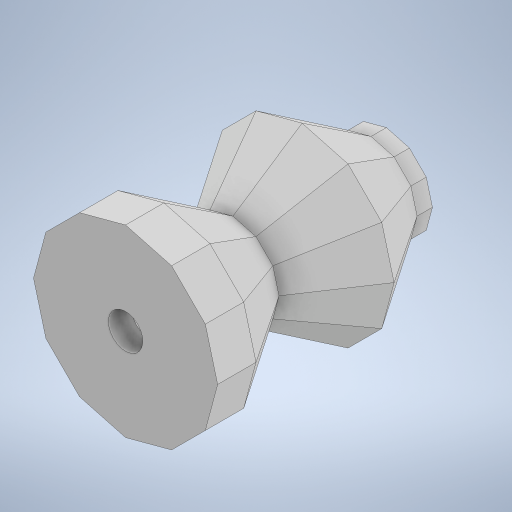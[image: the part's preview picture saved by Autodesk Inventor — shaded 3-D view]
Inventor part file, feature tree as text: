
AUTODESK INVENTOR PART (.ipt)
format: ipt  version: 2023 (Build 270158000, 158)  size: 354,304 bytes
history: native  units: in
note: dims shown in document units (in); Inventor stores cm internally (conversion verified against a paired STEP export)
features: sketch x6, extrude x4, projected_geometry x3, other x2, mirror x2, loft x1, shell x1
ambient origin geometry x8: Origin, YZ Plane, XZ Plane, XY Plane, X Axis, Y Axis, Z Axis, Center Point
bodies: Body1 (feature_tree)
feature tree (19):
  other  "솔리드1"
  sketch  "스케치1"
  other  "작업 평면1"
  loft  "로프트1"
  mirror  "미러1"
  mirror  "미러2"
  extrude  "돌출1"  Depth=0.3543in
  shell  "쉘7"  Thickness=0.4724in
  extrude  "돌출20"  TaperAngle=0.0deg  [1 undecoded]
  extrude  "돌출21"  TaperAngle=0.0deg  [1 undecoded]
  extrude  "돌출22"  Depth=0.1102in TaperAngle=0.0deg
  sketch  "스케치2"
  sketch  "스케치3"
  projected_geometry  "투영된 루프1"
  sketch  "스케치22"
  projected_geometry  "투영된 루프14"
  sketch  "스케치23"
  sketch  "스케치24"
  projected_geometry  "투영된 루프15"
note: 2 required parameter values undecoded (feature->parameter linkage not recoverable at this tier; creation-order binding heuristic only, values carry confidence <= 0.55)
